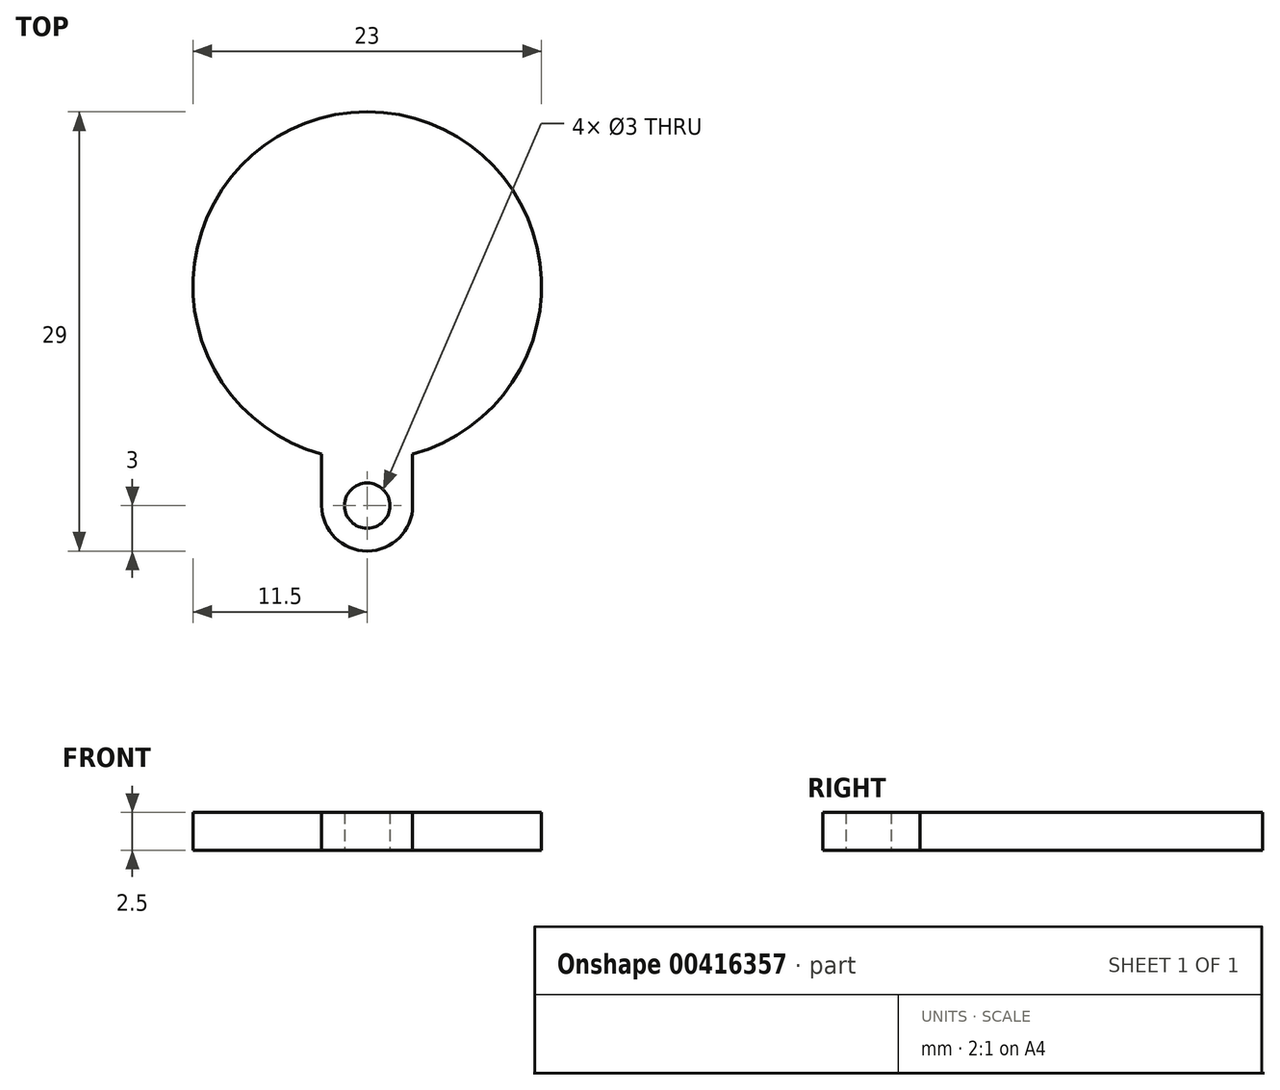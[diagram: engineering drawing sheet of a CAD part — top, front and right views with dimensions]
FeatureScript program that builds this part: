
annotation { "Feature Type Name" : "Feature", "Feature Type Description" : "" }
export const myFeature = defineFeature(function(context is Context, id is Id, definition is map)
    precondition{}
    {
        {
            var Q0;
            Q0=qCreatedBy(makeId("Top.planeOp"),FACE);
            var sketch = newSketch(context, id + "F0", { "sketchPlane" : qUnion([Q0])});
            skLineSegment(sketch, "E0", {"start": v(0, 0) * mm, "end": v(0, -25.14) * mm, "construction": true});
            skCircle(sketch, "E1", {"center": v(0, -14.5) * mm, "radius": 1.5 * mm});
            skLineSegment(sketch, "E2", {"start": v(0, 0) * mm, "end": v(0, 21.64) * mm, "construction": true});
            skLineSegment(sketch, "E3", {"start": v(0, -14.5) * mm, "end": v(-7.1, -14.5) * mm, "construction": true});
            skLineSegment(sketch, "E4", {"start": v(0, -14.5) * mm, "end": v(7.28, -14.5) * mm, "construction": true});
            skArc(sketch, "E5", {"start": v(-3, -14.5) * mm, "mid": v(0, -17.5) * mm, "end": v(3, -14.5) * mm});
            skArc(sketch, "E6", {"start": v(0, -11.5) * mm, "mid": v(1.51, -11.4) * mm, "end": v(3, -11.1) * mm, "construction": true});
            skArc(sketch, "E7", {"start": v(0, 11.5) * mm, "mid": v(-11.4, 1.51) * mm, "end": v(-3, -11.1) * mm});
            skLineSegment(sketch, "E8", {"start": v(-3, -14.5) * mm, "end": v(-3, -11.1) * mm});
            skLineSegment(sketch, "E9", {"start": v(3, -14.5) * mm, "end": v(3, -11.1) * mm});
            skArc(sketch, "E10", {"start": v(-3, -11.1) * mm, "mid": v(-1.51, -11.4) * mm, "end": v(0, -11.5) * mm, "construction": true});
            skArc(sketch, "E11", {"start": v(3, -11.1) * mm, "mid": v(11.4, 1.51) * mm, "end": v(0, 11.5) * mm});
            skSolve(sketch);
        }
        {
            var Q0;
            Q0=makeQuery(id+"F0.imprint","IMPRINT",FACE,{"disambiguationData":[TD([[makeQuery(id+"F0.imprint","IMPRINT",EDGE,{"derivedFrom":sQuery(id+"F0.wireOp",EDGE,"E1")}),-1.0]])]});
            extrude(context, id + "F1", {"entities" : qUnion([Q0]), "depth" : 2.5 * mm});
        }
    });
